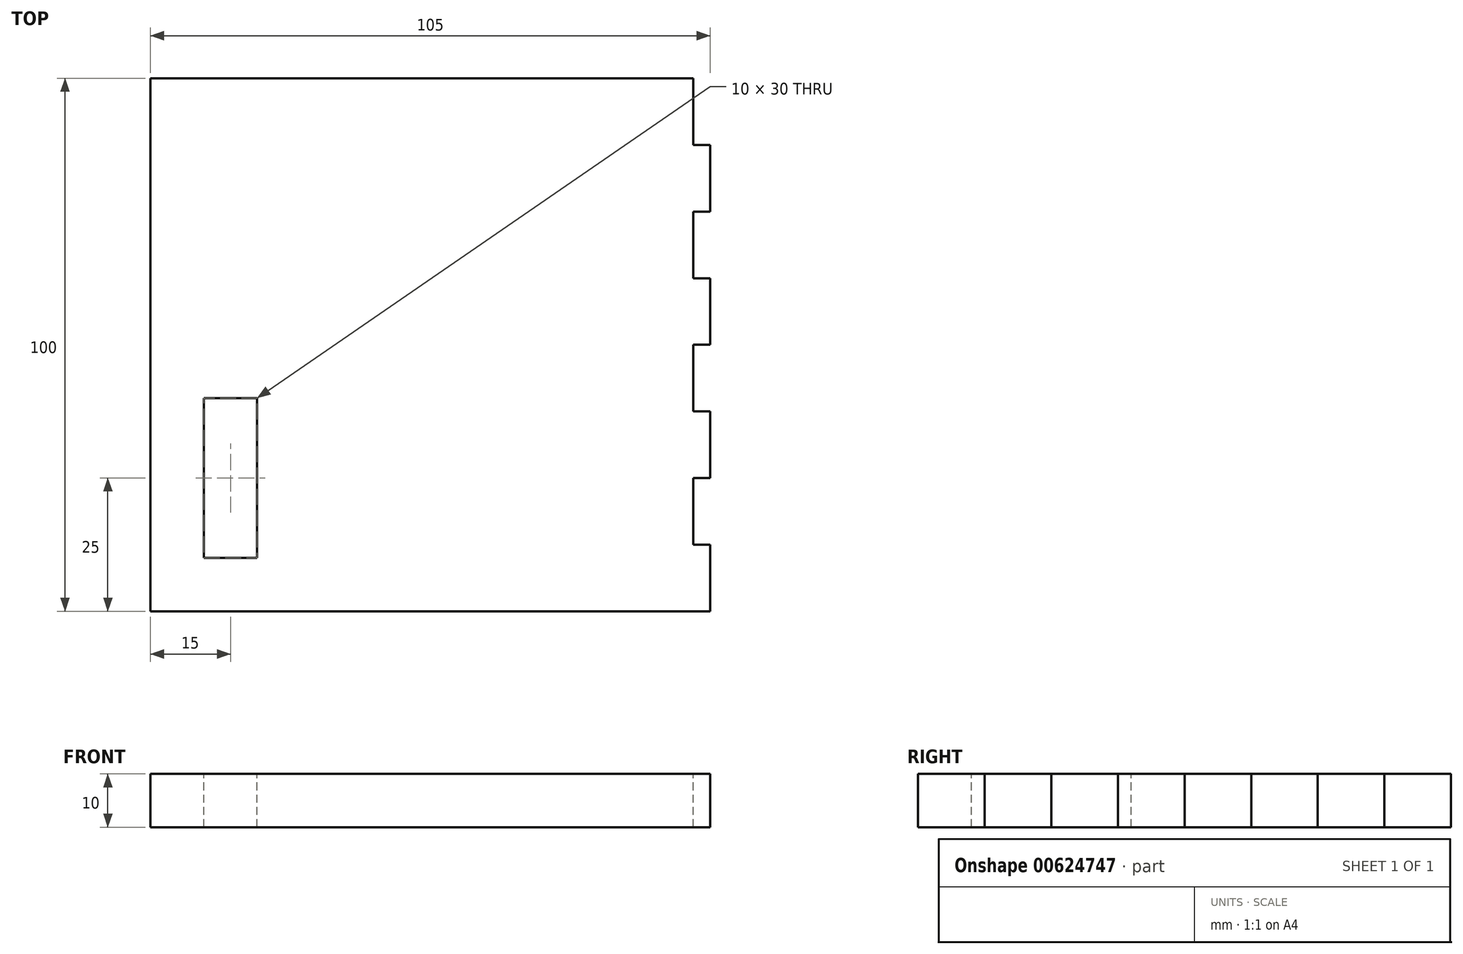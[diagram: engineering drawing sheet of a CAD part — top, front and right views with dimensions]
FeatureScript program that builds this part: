
annotation { "Feature Type Name" : "Feature", "Feature Type Description" : "" }
export const myFeature = defineFeature(function(context is Context, id is Id, definition is map)
    precondition{}
    {
        {
            var Q0;
            Q0=qCreatedBy(makeId("Top.planeOp"),FACE);
            var sketch = newSketch(context, id + "F0", { "sketchPlane" : qUnion([Q0])});
            skLineSegment(sketch, "E0.bottom", {"start": v(60, 50) * mm, "end": v(-60, 50) * mm});
            skLineSegment(sketch, "E0.top", {"start": v(60, -50) * mm, "end": v(-60, -50) * mm});
            skLineSegment(sketch, "E0.left", {"start": v(60, 50) * mm, "end": v(60, -50) * mm});
            skLineSegment(sketch, "E0.right", {"start": v(-60, 50) * mm, "end": v(-60, -50) * mm});
            skPoint(sketch, "E0.middle", {"position": v(0, 0) * mm});
            skSolve(sketch);
        }
        {
            var Q0;
            Q0 = qSketchRegion(id + "F0", true);
            extrude(context, id + "F1", {"entities" : qUnion([Q0]), "depth" : 10 * mm, "offsetDistance" : 25 * mm});
        }
        {
            var Q0;
            Q0=makeQuery(id+"F1.opExtrude","CAP_FACE",FACE,{"disambiguationData":[OSD([sQuery(id+"F0.wireOp",EDGE,"E0.bottom"),sQuery(id+"F0.wireOp",EDGE,"E0.top"),sQuery(id+"F0.wireOp",EDGE,"E0.left"),sQuery(id+"F0.wireOp",EDGE,"E0.right")])],"isStart":false});
            var sketch = newSketch(context, id + "F2", { "sketchPlane" : qUnion([Q0])});
            skLineSegment(sketch, "E1.bottom", {"start": v(-40, -10) * mm, "end": v(-50, -10) * mm});
            skLineSegment(sketch, "E1.top", {"start": v(-40, -40) * mm, "end": v(-50, -40) * mm});
            skLineSegment(sketch, "E1.left", {"start": v(-40, -10) * mm, "end": v(-40, -40) * mm});
            skLineSegment(sketch, "E1.right", {"start": v(-50, -10) * mm, "end": v(-50, -40) * mm});
            skPoint(sketch, "E1.middle", {"position": v(-45, -25) * mm});
            skSolve(sketch);
        }
        {
            var Q0;
            Q0 = qSketchRegion(id + "F2", true);
            extrude(context, id + "F3", {"entities" : qUnion([Q0]), "operationType" : NewBodyOperationType.REMOVE, "endBound" : BoundingType.THROUGH_ALL, "oppositeDirection" : true, "depth" : 25 * mm, "offsetDistance" : 25 * mm});
        }
        {
            var Q0;
            Q0=makeQuery(id+"F1.opExtrude","CAP_FACE",FACE,{"disambiguationData":[OSD([sQuery(id+"F0.wireOp",EDGE,"E0.bottom"),sQuery(id+"F0.wireOp",EDGE,"E0.top"),sQuery(id+"F0.wireOp",EDGE,"E0.left"),sQuery(id+"F0.wireOp",EDGE,"E0.right")])],"isStart":false});
            var sketch = newSketch(context, id + "F4", { "sketchPlane" : qUnion([Q0])});
            skLineSegment(sketch, "E2.bottom", {"start": v(60, -50) * mm, "end": v(45, -50) * mm});
            skLineSegment(sketch, "E2.top", {"start": v(60, 50) * mm, "end": v(41.83, 50) * mm});
            skLineSegment(sketch, "E2.left", {"start": v(60, -50) * mm, "end": v(60, 50) * mm});
            skLineSegment(sketch, "E2.right", {"start": v(45, -50) * mm, "end": v(45, -37.5) * mm});
            skLineSegment(sketch, "E3", {"start": v(45, 0) * mm, "end": v(45, 12.5) * mm});
            skLineSegment(sketch, "E4", {"start": v(45, -25) * mm, "end": v(45, -12.5) * mm});
            skLineSegment(sketch, "E5", {"start": v(45, 25) * mm, "end": v(45, 37.5) * mm});
            skLineSegment(sketch, "E6", {"start": v(41.83, -37.5) * mm, "end": v(45, -37.5) * mm});
            skLineSegment(sketch, "E7", {"start": v(41.83, -37.5) * mm, "end": v(41.83, -25) * mm});
            skLineSegment(sketch, "E8", {"start": v(41.83, 37.5) * mm, "end": v(45, 37.5) * mm});
            skLineSegment(sketch, "E9", {"start": v(41.83, 25) * mm, "end": v(45, 25) * mm});
            skLineSegment(sketch, "E10", {"start": v(41.83, 12.5) * mm, "end": v(45, 12.5) * mm});
            skLineSegment(sketch, "E11", {"start": v(41.83, -12.5) * mm, "end": v(45, -12.5) * mm});
            skLineSegment(sketch, "E12", {"start": v(41.83, 0) * mm, "end": v(45, 0) * mm});
            skLineSegment(sketch, "E13", {"start": v(41.83, -25) * mm, "end": v(45, -25) * mm});
            skLineSegment(sketch, "E14.trimOffspring", {"start": v(41.83, -12.5) * mm, "end": v(41.83, 0) * mm});
            skLineSegment(sketch, "E15.trimOffspring", {"start": v(41.83, 12.5) * mm, "end": v(41.83, 25) * mm});
            skLineSegment(sketch, "E16.trimOffspring", {"start": v(41.83, 37.5) * mm, "end": v(41.83, 50) * mm});
            skPoint(sketch, "E17.orphan", {"position": v(45, 50) * mm});
            skSolve(sketch);
        }
        {
            var Q0;
            Q0 = qSketchRegion(id + "F4", true);
            extrude(context, id + "F5", {"entities" : qUnion([Q0]), "operationType" : NewBodyOperationType.REMOVE, "oppositeDirection" : true, "depth" : 25 * mm, "offsetDistance" : 25 * mm});
        }
    });
